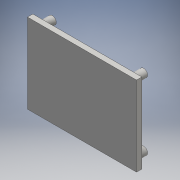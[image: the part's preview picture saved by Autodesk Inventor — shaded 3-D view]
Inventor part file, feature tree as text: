
AUTODESK INVENTOR PART (.ipt)
format: ipt  version: 2016 (Build 200138000, 138)  size: 138,752 bytes
history: native  units: mm
features: sketch x3, extrude x2, hole x1
ambient origin geometry x8: Origin, YZ Plane, XZ Plane, XY Plane, X Axis, Y Axis, Z Axis, Center Point
bodies: Solid1 (feature_tree)
feature tree (6):
  extrude  "Extrusion1"  Depth=45.0mm
  hole  "Hole1"  [1 undecoded]
  extrude  "Extrusion2"  Depth=6.0mm
  sketch  "Sketch1"  dims[d0=61.5mm d1=45.0mm]
  sketch  "Sketch2"  dims[d2=3.0mm d3=0.0mm d4=5.0mm]
  sketch  "Sketch3"  dims[d5=27.0mm d8=5.0mm d9=12.0mm d10=5.0mm d11=18.0mm d12=5.0mm d13=7.5mm d14=7.5mm d15=18.0mm d16=5.0mm d17=6.0mm d18=4.0mm d19=2.0mm d20=90.0deg d21=2.5mm d22=0.0mm d23=4.5mm d24=3.5mm d25=5.0mm d26=4.5mm d27=3.5mm d28=5.0mm d29=4.5mm d30=3.5mm d31=4.5mm d32=4.5mm d33=24.5mm d34=5.0mm d35=5.0mm d36=3.5mm d37=4.5mm d38=20.0mm d39=6.0mm d40=0.0mm]
note: 1 required parameter value undecoded (feature->parameter linkage not recoverable at this tier; creation-order binding heuristic only, values carry confidence <= 0.55)
